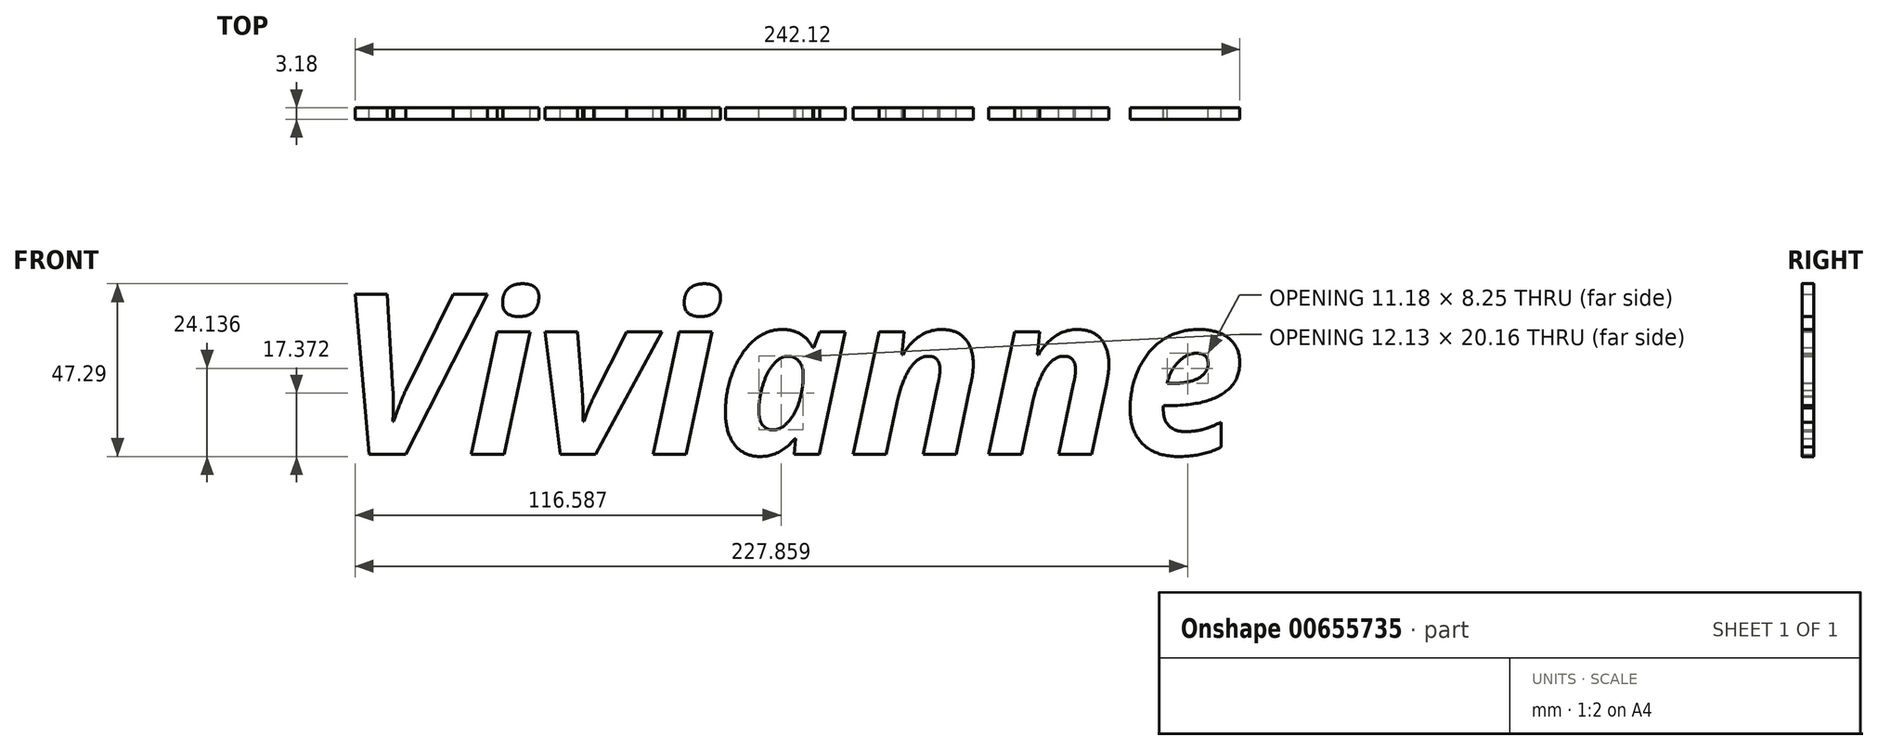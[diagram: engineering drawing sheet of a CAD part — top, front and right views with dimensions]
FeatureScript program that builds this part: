
annotation { "Feature Type Name" : "Feature", "Feature Type Description" : "" }
export const myFeature = defineFeature(function(context is Context, id is Id, definition is map)
    precondition{}
    {
        {
            var Q0;
            Q0=qCreatedBy(makeId("Front.planeOp"),FACE);
            var sketch = newSketch(context, id + "F0", { "sketchPlane" : qUnion([Q0])});
            skText(sketch, "E0", { "text": "Vivianne", "fontName": "OpenSans-BoldItalic.ttf"});
            const initialGuessF0  = {"E0": [-0.05495, -0.0632, 1, 0, 0.04424]};
            skSetInitialGuess(sketch, initialGuessF0);
            skSolve(sketch);
        }
        {
            var Q0;
            Q0 = qSketchRegion(id + "F0", true);
            extrude(context, id + "F1", {"entities" : qUnion([Q0]), "depth" : 3.17 * mm, "offsetDistance" : 25.4 * mm});
        }
    });
